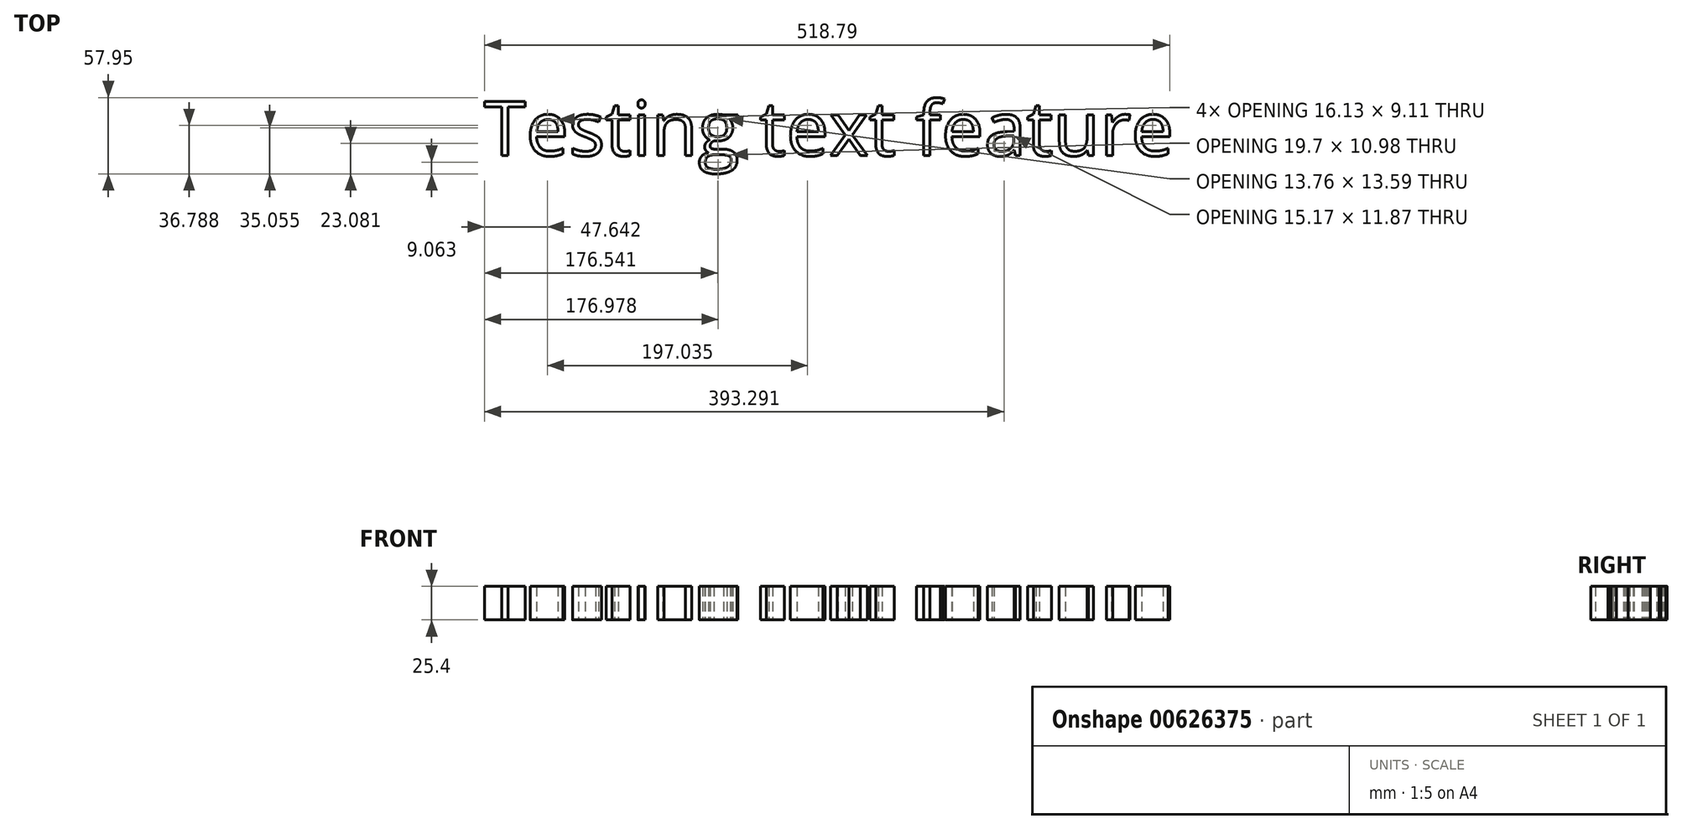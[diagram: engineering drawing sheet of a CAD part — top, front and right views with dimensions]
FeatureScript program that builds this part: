
annotation { "Feature Type Name" : "Feature", "Feature Type Description" : "" }
export const myFeature = defineFeature(function(context is Context, id is Id, definition is map)
    precondition{}
    {
        {
            var Q0;
            Q0=qCreatedBy(makeId("Top.planeOp"),FACE);
            var sketch = newSketch(context, id + "F0", { "sketchPlane" : qUnion([Q0])});
            skText(sketch, "E0", { "text": "Testing text feature", "fontName": "OpenSans-Regular.ttf"});
            const initialGuessF0  = {"E0": [-0.22372, -0.0324, 1, 0, 0.0415]};
            skSetInitialGuess(sketch, initialGuessF0);
            skSolve(sketch);
        }
        {
            var Q0;
            Q0 = qSketchRegion(id + "F0", true);
            extrude(context, id + "F1", {"entities" : qUnion([Q0]), "depth" : 25.4 * mm, "offsetDistance" : 25.4 * mm});
        }
    });
